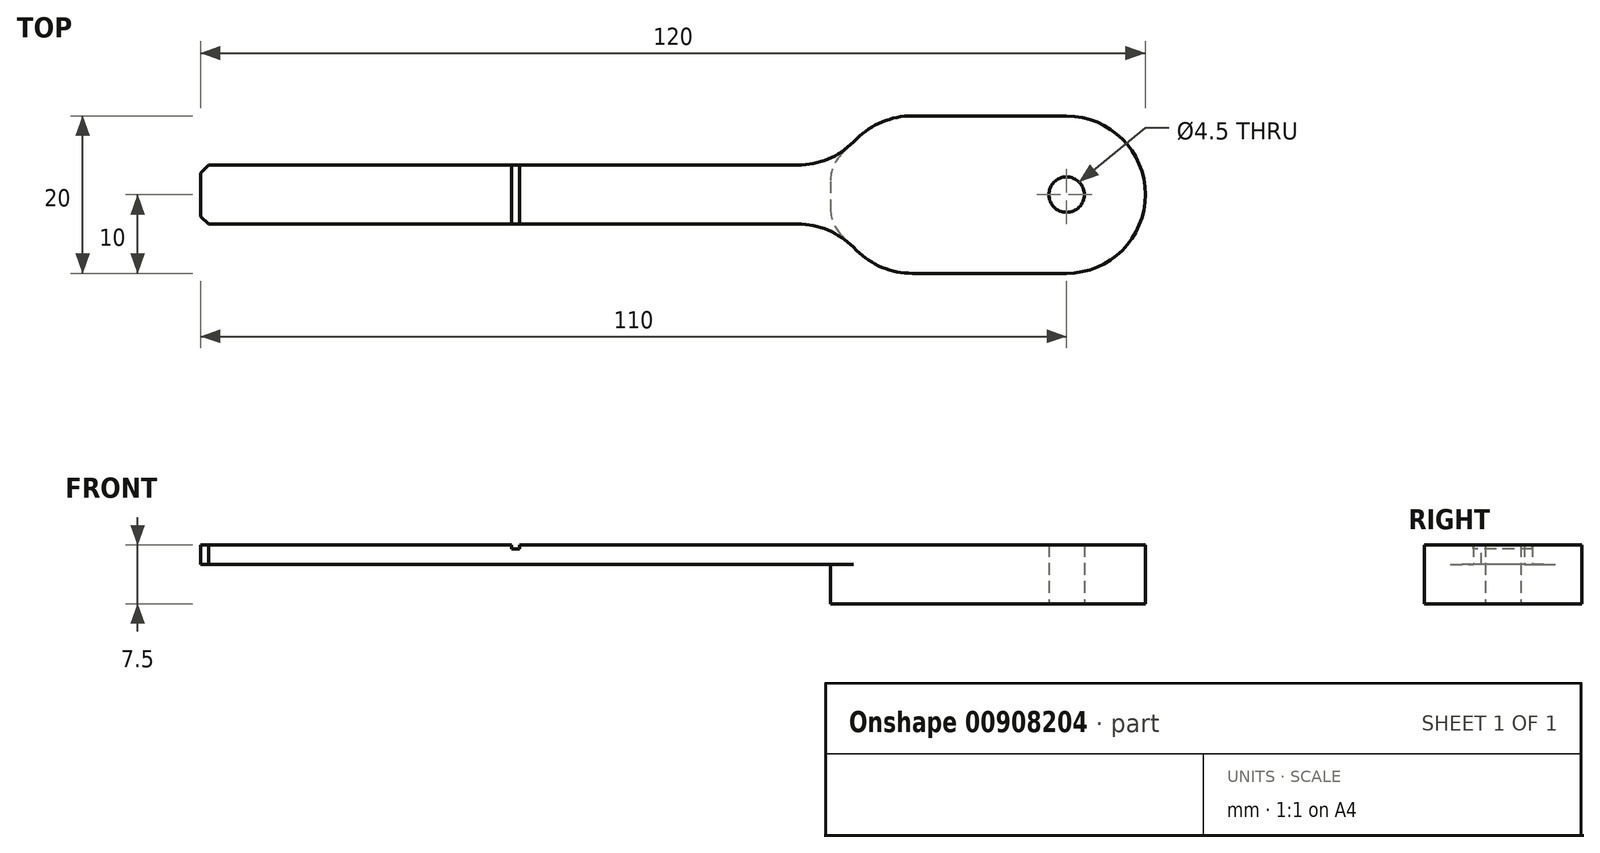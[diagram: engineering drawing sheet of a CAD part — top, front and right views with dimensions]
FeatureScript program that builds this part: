
annotation { "Feature Type Name" : "Feature", "Feature Type Description" : "" }
export const myFeature = defineFeature(function(context is Context, id is Id, definition is map)
    precondition{}
    {
        {
            var Q0;
            Q0=qCreatedBy(makeId("Top.planeOp"),FACE);
            var sketch = newSketch(context, id + "F0", { "sketchPlane" : qUnion([Q0])});
            skLineSegment(sketch, "E0.bottom", {"start": v(-40, 3.75) * mm, "end": v(40, 3.75) * mm});
            skLineSegment(sketch, "E0.top", {"start": v(-40, -3.75) * mm, "end": v(40, -3.75) * mm});
            skLineSegment(sketch, "E0.left", {"start": v(-40, 3.75) * mm, "end": v(-40, -3.75) * mm});
            skLineSegment(sketch, "E0.right", {"start": v(40, 3.75) * mm, "end": v(40, -3.75) * mm});
            skPoint(sketch, "E0.middle", {"position": v(0, 0) * mm});
            skLineSegment(sketch, "E1", {"start": v(-40, 0) * mm, "end": v(0, 0) * mm, "construction": true});
            skLineSegment(sketch, "E2", {"start": v(40, 3.75) * mm, "end": v(46.25, 10) * mm});
            skLineSegment(sketch, "E3", {"start": v(46.25, 10) * mm, "end": v(70, 10) * mm});
            skLineSegment(sketch, "E4", {"start": v(40, 0) * mm, "end": v(311.31, 0) * mm, "construction": true});
            skLineSegment(sketch, "E5", {"start": v(70, -10) * mm, "end": v(46.25, -10) * mm});
            skLineSegment(sketch, "E6", {"start": v(46.25, -10) * mm, "end": v(40, -3.75) * mm});
            skCircle(sketch, "E7", {"center": v(70, 0) * mm, "radius": 2.25 * mm});
            skArc(sketch, "E8", {"start": v(70, 10) * mm, "mid": v(80, 0) * mm, "end": v(70, -10) * mm});
            skSolve(sketch);
        }
        {
            var Q0;
            Q0=qSketchRegion(id+"F0",true);
            extrude(context, id + "F1", {"entities" : qUnion([Q0]), "depth" : 2.5 * mm, "offsetDistance" : 25 * mm});
        }
        {
            var Q0;
            Q0=makeQuery(id+"F0.imprint","IMPRINT",FACE,{"disambiguationData":[TD([[makeQuery(id+"F0.imprint","IMPRINT",EDGE,{"derivedFrom":sQuery(id+"F0.wireOp",EDGE,"E0.right")}),1.0]])]});
            extrude(context, id + "F2", {"entities" : qUnion([Q0]), "operationType" : NewBodyOperationType.ADD, "oppositeDirection" : true, "depth" : 5 * mm, "offsetDistance" : 25 * mm});
        }
        {
            var Q0;
            Q0=makeQuery(id+"F1.opExtrude","SWEPT_EDGE",EDGE,{"disambiguationData":[OSD([sQuery(id+"F0.wireOp",EDGE,"E0.top"),sQuery(id+"F0.wireOp",EDGE,"E0.left")])]});
            var Q1;
            Q1=makeQuery(id+"F1.opExtrude","SWEPT_EDGE",EDGE,{"disambiguationData":[OSD([sQuery(id+"F0.wireOp",EDGE,"E0.bottom"),sQuery(id+"F0.wireOp",EDGE,"E0.left")])]});
            chamfer(context, id + "F3", {"entities" : qUnion([Q0, Q1]), "width" : 1 * mm, "tangentPropagation" : true});
        }
        {
            var Q0;
            Q0=makeQuery(id+"F1.opExtrude","SWEPT_EDGE",EDGE,{"disambiguationData":[OSD([sQuery(id+"F0.wireOp",EDGE,"E0.top"),sQuery(id+"F0.wireOp",EDGE,"E0.right"),sQuery(id+"F0.wireOp",EDGE,"E6")])]});
            var Q1;
            {var subQ0=sQuery(id+"F0.wireOp",EDGE,"E6");var subQ1=sQuery(id+"F0.wireOp",EDGE,"E5");Q1=makeQuery(id+"F2.boolean.opBoolean","MERGE",EDGE,{"derivedFrom":[makeQuery(id+"F1.opExtrude","SWEPT_EDGE",EDGE,{"disambiguationData":[OSD([subQ1,subQ0])]}),makeQuery(id+"F2.opExtrude","SWEPT_EDGE",EDGE,{"disambiguationData":[OSD([subQ1,subQ0])]})]});}
            var Q2;
            {var subQ0=sQuery(id+"F0.wireOp",EDGE,"E3");var subQ1=sQuery(id+"F0.wireOp",EDGE,"E2");Q2=makeQuery(id+"F2.boolean.opBoolean","MERGE",EDGE,{"derivedFrom":[makeQuery(id+"F1.opExtrude","SWEPT_EDGE",EDGE,{"disambiguationData":[OSD([subQ1,subQ0])]}),makeQuery(id+"F2.opExtrude","SWEPT_EDGE",EDGE,{"disambiguationData":[OSD([subQ1,subQ0])]})]});}
            var Q3;
            Q3=makeQuery(id+"F1.opExtrude","SWEPT_EDGE",EDGE,{"disambiguationData":[OSD([sQuery(id+"F0.wireOp",EDGE,"E0.bottom"),sQuery(id+"F0.wireOp",EDGE,"E0.right"),sQuery(id+"F0.wireOp",EDGE,"E2")])]});
            fillet(context, id + "F4", {"entities" : qUnion([Q0, Q1, Q2, Q3]), "tangentPropagation" : true, "radius" : 10 * mm, "defaultsChanged" : true, "vertexSettings" : [], "allowEdgeOverflow" : false});
        }
        {
            var Q0;
            Q0=makeQuery(id+"F2.opExtrude","SWEPT_EDGE",EDGE,{"disambiguationData":[OSD([sQuery(id+"F0.wireOp",EDGE,"E0.top"),sQuery(id+"F0.wireOp",EDGE,"E0.right"),sQuery(id+"F0.wireOp",EDGE,"E6")])]});
            var Q1;
            Q1=makeQuery(id+"F2.opExtrude","SWEPT_EDGE",EDGE,{"disambiguationData":[OSD([sQuery(id+"F0.wireOp",EDGE,"E0.bottom"),sQuery(id+"F0.wireOp",EDGE,"E0.right"),sQuery(id+"F0.wireOp",EDGE,"E2")])]});
            fillet(context, id + "F5", {"entities" : qUnion([Q0, Q1]), "tangentPropagation" : true, "radius" : 5 * mm, "defaultsChanged" : false, "vertexSettings" : [], "allowEdgeOverflow" : false});
        }
        {
            var Q0;
            Q0=makeQuery(id+"F1.opExtrude","CAP_FACE",FACE,{"disambiguationData":[OSD([sQuery(id+"F0.wireOp",EDGE,"E0.bottom"),sQuery(id+"F0.wireOp",EDGE,"E0.top"),sQuery(id+"F0.wireOp",EDGE,"E0.left"),sQuery(id+"F0.wireOp",EDGE,"E2"),sQuery(id+"F0.wireOp",EDGE,"E3"),sQuery(id+"F0.wireOp",EDGE,"E5"),sQuery(id+"F0.wireOp",EDGE,"E6"),sQuery(id+"F0.wireOp",EDGE,"E7"),sQuery(id+"F0.wireOp",EDGE,"E8")])],"isStart":false});
            var sketch = newSketch(context, id + "F6", { "sketchPlane" : qUnion([Q0])});
            skLineSegment(sketch, "E9.bottom", {"start": v(-0.5, -3.75) * mm, "end": v(0.5, -3.75) * mm});
            skLineSegment(sketch, "E9.top", {"start": v(-0.5, 3.75) * mm, "end": v(0.5, 3.75) * mm});
            skLineSegment(sketch, "E9.left", {"start": v(-0.5, 3.75) * mm, "end": v(-0.5, -3.75) * mm});
            skLineSegment(sketch, "E9.right", {"start": v(0.5, 3.75) * mm, "end": v(0.5, -3.75) * mm});
            skPoint(sketch, "E9.middle", {"position": v(0, 0) * mm});
            skSolve(sketch);
        }
        {
            var Q0;
            Q0 = qSketchRegion(id + "F6", true);
            extrude(context, id + "F7", {"entities" : qUnion([Q0]), "operationType" : NewBodyOperationType.REMOVE, "oppositeDirection" : true, "depth" : 0.5 * mm, "offsetDistance" : 25 * mm});
        }
    });
